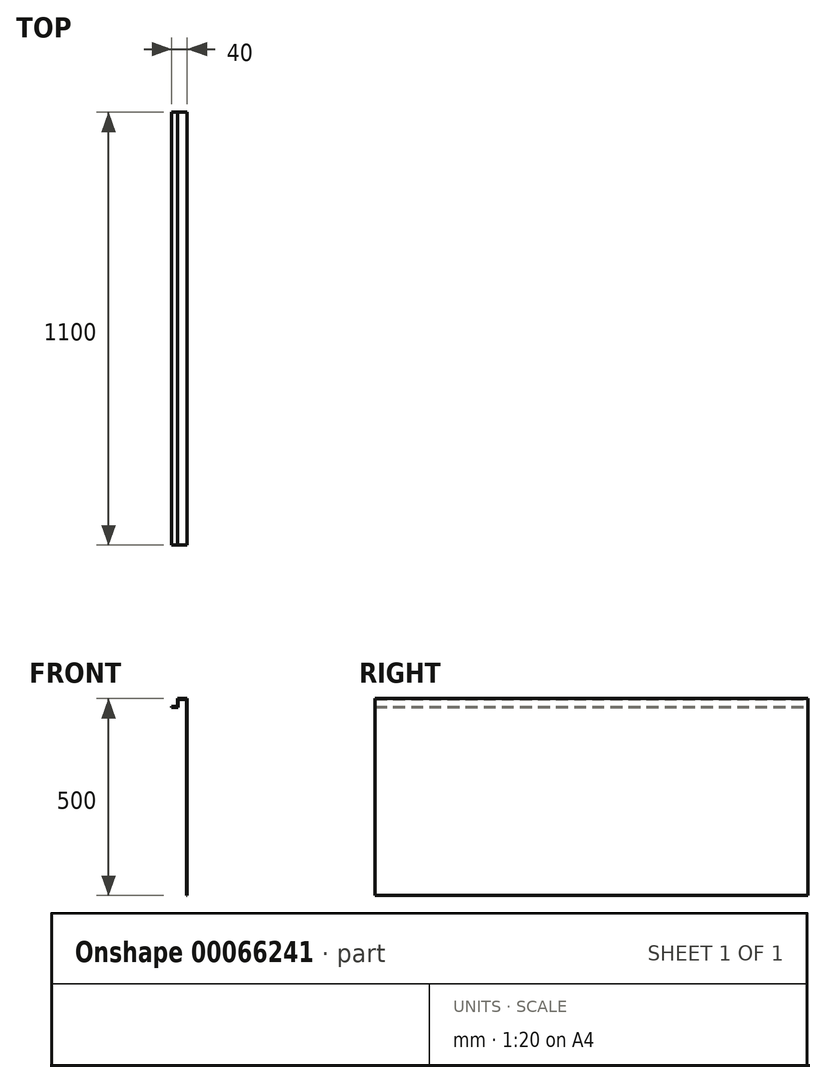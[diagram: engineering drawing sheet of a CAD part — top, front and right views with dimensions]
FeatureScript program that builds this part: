
annotation { "Feature Type Name" : "Feature", "Feature Type Description" : "" }
export const myFeature = defineFeature(function(context is Context, id is Id, definition is map)
    precondition{}
    {
        {
            var Q0;
            Q0=qCreatedBy(makeId("Front.planeOp"),FACE);
            var sketch = newSketch(context, id + "F0", { "sketchPlane" : qUnion([Q0])});
            skLineSegment(sketch, "E0", {"start": v(-30.46, 35.36) * mm, "end": v(-15.46, 35.36) * mm});
            skLineSegment(sketch, "E1", {"start": v(-15.46, 35.36) * mm, "end": v(-15.46, 55.36) * mm});
            skLineSegment(sketch, "E2", {"start": v(-15.46, 55.36) * mm, "end": v(9.54, 55.36) * mm});
            skLineSegment(sketch, "E3", {"start": v(9.54, 55.36) * mm, "end": v(9.54, -444.64) * mm});
            skLineSegment(sketch, "E4.0", {"start": v(-30.46, 33.36) * mm, "end": v(-13.46, 33.36) * mm});
            skLineSegment(sketch, "E5.0", {"start": v(-13.46, 33.36) * mm, "end": v(-13.46, 53.36) * mm});
            skLineSegment(sketch, "E6.0", {"start": v(-13.46, 53.36) * mm, "end": v(7.54, 53.36) * mm});
            skLineSegment(sketch, "E7.0", {"start": v(7.54, 53.36) * mm, "end": v(7.54, -444.64) * mm});
            skLineSegment(sketch, "E8", {"start": v(-30.46, 33.36) * mm, "end": v(-30.46, 35.36) * mm});
            skLineSegment(sketch, "E9", {"start": v(7.54, -444.64) * mm, "end": v(9.54, -444.64) * mm});
            skSolve(sketch);
        }
        {
            var Q0;
            {var subQ5=sQuery(id+"F0.wireOp",EDGE,"E0");Q0=makeQuery(id+"F0.imprint","IMPRINT",FACE,{"disambiguationData":[TD([[makeQuery(id+"F0.imprint","IMPRINT",EDGE,{"derivedFrom":subQ5}),-1.0]])]});}
            var Q1;
            {var subQ0=sQuery(id+"F0.wireOp",EDGE,"E9");Q1=makeQuery(id+"F0.imprint","IMPRINT",FACE,{"disambiguationData":[TD([[makeQuery(id+"F0.imprint","IMPRINT",EDGE,{"derivedFrom":subQ0}),1.0]])]});}
            var Q2;
            {var subQ0=sQuery(id+"F0.wireOp",EDGE,"E5.0");var subQ1=sQuery(id+"F0.wireOp",EDGE,"E2");var subQ2=makeQuery(id+"F0.imprint","INTERSECT",VERTEX,{"derivedFrom":[subQ1,subQ0]});Q2=makeQuery(id+"F0.imprint","IMPRINT",FACE,{"disambiguationData":[TD([[makeQuery(id+"F0.imprint","IMPRINT",EDGE,{"disambiguationData":[TD([[subQ2,-1.0]])],"derivedFrom":subQ1}),-1.0]])]});}
            var Q3;
            {var subQ0=sQuery(id+"F0.wireOp",EDGE,"E2");var subQ1=sQuery(id+"F0.wireOp",EDGE,"E1");var subQ2=makeQuery(id+"F0.imprint","INTERSECT",VERTEX,{"derivedFrom":[subQ1,subQ0]});Q3=makeQuery(id+"F0.imprint","IMPRINT",FACE,{"disambiguationData":[TD([[makeQuery(id+"F0.imprint","IMPRINT",EDGE,{"disambiguationData":[TD([[subQ2,1.0]])],"derivedFrom":subQ1}),-1.0]])]});}
            var Q4;
            {var subQ0=sQuery(id+"F0.wireOp",EDGE,"E3");var subQ1=sQuery(id+"F0.wireOp",EDGE,"E2");var subQ2=makeQuery(id+"F0.imprint","INTERSECT",VERTEX,{"derivedFrom":[subQ1,subQ0]});Q4=makeQuery(id+"F0.imprint","IMPRINT",FACE,{"disambiguationData":[TD([[makeQuery(id+"F0.imprint","IMPRINT",EDGE,{"disambiguationData":[TD([[subQ2,1.0]])],"derivedFrom":subQ1}),-1.0]])]});}
            extrude(context, id + "F1", {"entities" : qUnion([Q0, Q1, Q2, Q3, Q4]), "depth" : 1100 * mm});
        }
    });
